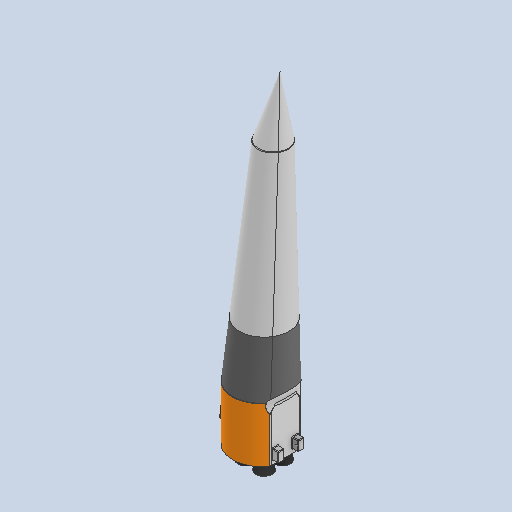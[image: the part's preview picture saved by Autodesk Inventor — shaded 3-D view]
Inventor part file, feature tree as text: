
AUTODESK INVENTOR PART (.ipt)
format: ipt  version: 2023 (Build 270158030, 158C)  size: 891,904 bytes
history: native  units: mm
features: other x4, split x1, sketch x1
ambient origin geometry x8: Origin, YZ Plane, XZ Plane, XY Plane, X Axis, Y Axis, Z Axis, Center Point
bodies: Solid2 (feature_tree), Solid3 (feature_tree)
feature tree (6):
  other  "Soyuz Model.ipt"
  split  "Split1"
  other  "Soyuz Booster::Soyuz Model.ipt"
  other  "TaggingFeature1"
  sketch  "Sketch1"  dims[d0=10.0mm d1=55.0mm]
  other  "Soyuz Booster"
